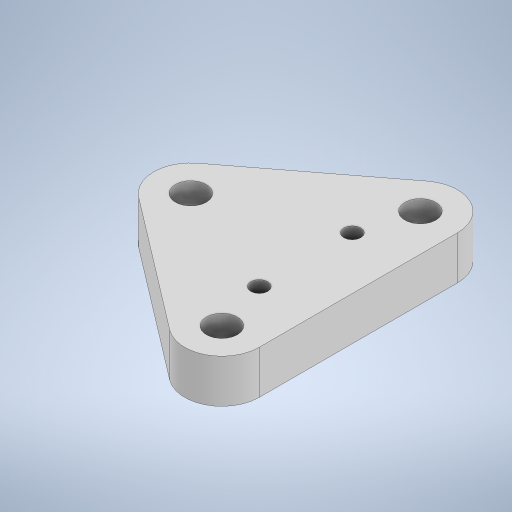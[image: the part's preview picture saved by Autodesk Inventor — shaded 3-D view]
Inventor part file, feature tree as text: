
AUTODESK INVENTOR PART (.ipt)
format: ipt  version: 2023.2 (Build 272271030, 271C)  size: 258,048 bytes
history: native  units: mm
features: extrude x2, sketch x2, projected_geometry x1
ambient origin geometry x8: Origin, YZ Plane, XZ Plane, XY Plane, X Axis, Y Axis, Z Axis, Center Point
bodies: Solid1 (feature_tree)
feature tree (5):
  extrude  "Extrusion1"  Depth=10.0mm
  extrude  "Extrusion2"  Depth=5.0mm
  sketch  "Sketch1"  dims[d0=10.0mm d1=64.0mm]
  sketch  "Sketch3"  dims[d2=32.0mm d3=24.0mm d4=42.0mm d5=14.0mm d6=0.0mm d7=10.0mm d8=40.0mm d9=5.5mm d10=5.0mm d11=6.95mm d12=0.0mm d13=0.0mm]
  projected_geometry  "Projected Loop1"
